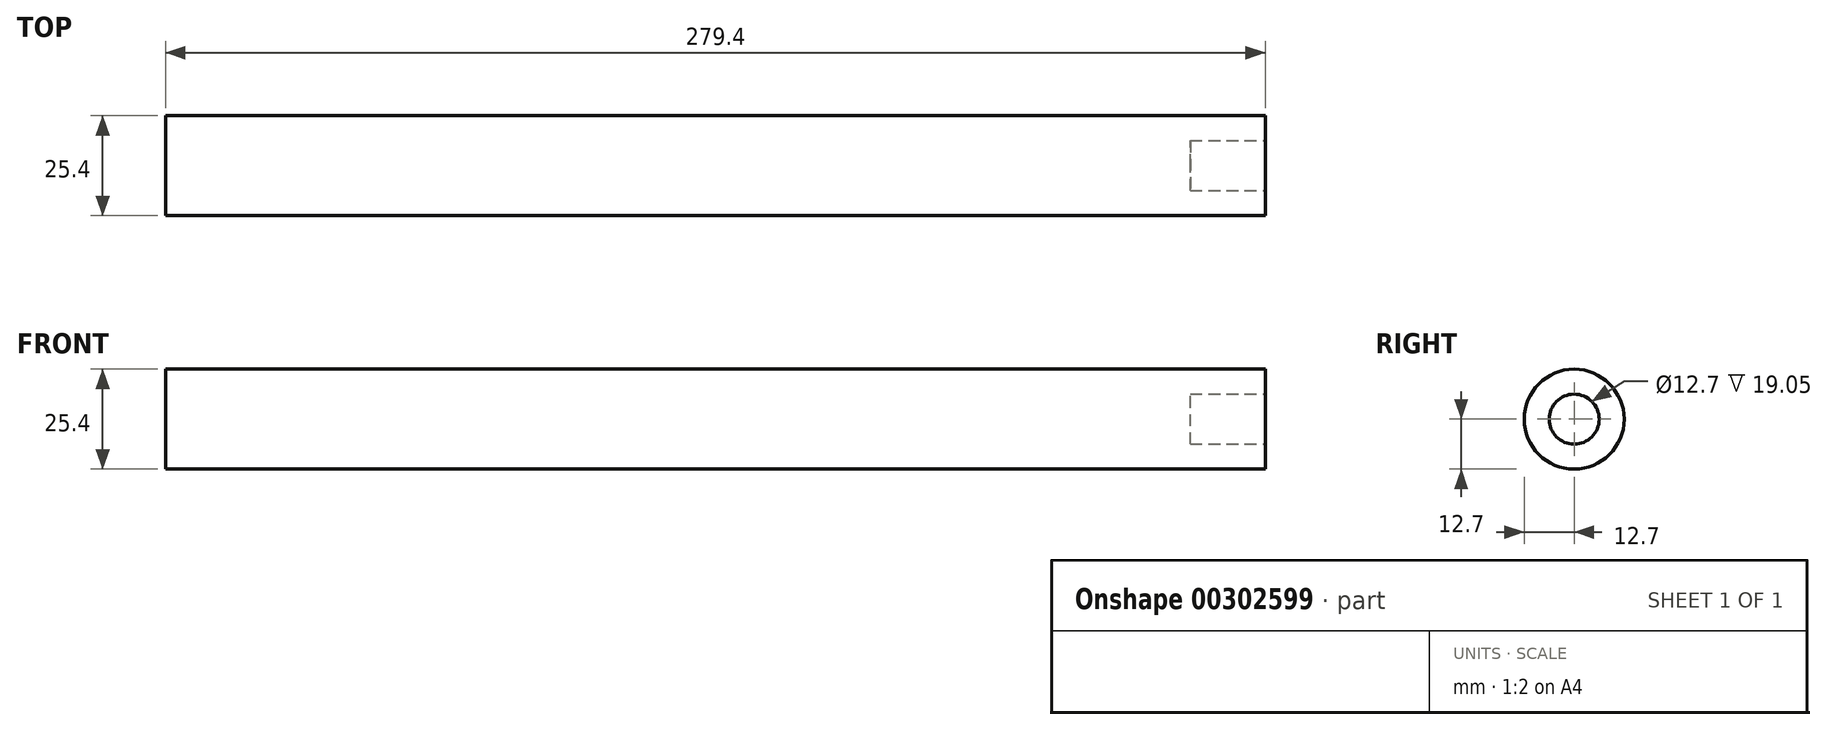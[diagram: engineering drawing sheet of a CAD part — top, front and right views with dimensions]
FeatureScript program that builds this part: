
annotation { "Feature Type Name" : "Feature", "Feature Type Description" : "" }
export const myFeature = defineFeature(function(context is Context, id is Id, definition is map)
    precondition{}
    {
        {
            var Q0;
            Q0=qCreatedBy(makeId("Right.planeOp"),FACE);
            var sketch = newSketch(context, id + "F0", { "sketchPlane" : qUnion([Q0])});
            skCircle(sketch, "E0", {"center": v(0, 0) * mm, "radius": 12.7 * mm});
            skSolve(sketch);
        }
        {
            var Q0;
            Q0=makeQuery(id+"F0.imprint","IMPRINT",FACE,{"disambiguationData":[TD([[makeQuery(id+"F0.imprint","IMPRINT",EDGE,{"derivedFrom":sQuery(id+"F0.wireOp",EDGE,"E0")}),1.0]])]});
            extrude(context, id + "F1", {"entities" : qUnion([Q0]), "depth" : 279.4 * mm});
        }
        {
            var Q0;
            Q0=makeQuery(id+"F1.opExtrude","CAP_FACE",FACE,{"disambiguationData":[OSD([sQuery(id+"F0.wireOp",EDGE,"E0")])],"isStart":false});
            var sketch = newSketch(context, id + "F2", { "sketchPlane" : qUnion([Q0])});
            skCircle(sketch, "E1", {"center": v(0, 0) * mm, "radius": 6.35 * mm});
            skSolve(sketch);
        }
        {
            var Q0;
            Q0=makeQuery(id+"F2.imprint","IMPRINT",FACE,{"disambiguationData":[TD([[makeQuery(id+"F2.imprint","IMPRINT",EDGE,{"derivedFrom":sQuery(id+"F2.wireOp",EDGE,"E1")}),1.0]])]});
            extrude(context, id + "F3", {"entities" : qUnion([Q0]), "operationType" : NewBodyOperationType.REMOVE, "oppositeDirection" : true, "depth" : 19.05 * mm});
        }
        {
            var Q0;
            Q0=makeQuery(id+"F1.opExtrude","CAP_FACE",FACE,{"disambiguationData":[OSD([sQuery(id+"F0.wireOp",EDGE,"E0")])],"isStart":false});
            var sketch = newSketch(context, id + "F4", { "sketchPlane" : qUnion([Q0])});
            skLineSegment(sketch, "E2.bottom", {"start": v(-2.54, 12.7) * mm, "end": v(2.54, 12.7) * mm});
            skLineSegment(sketch, "E2.top", {"start": v(-2.54, -19.69) * mm, "end": v(2.54, -19.69) * mm});
            skLineSegment(sketch, "E2.left", {"start": v(-2.54, 12.7) * mm, "end": v(-2.54, -19.69) * mm});
            skLineSegment(sketch, "E2.right", {"start": v(2.54, 12.7) * mm, "end": v(2.54, -19.69) * mm});
            skLineSegment(sketch, "E3.bottom", {"start": v(-12.7, 2.54) * mm, "end": v(19.69, 2.54) * mm});
            skLineSegment(sketch, "E3.top", {"start": v(-12.7, -2.54) * mm, "end": v(19.69, -2.54) * mm});
            skLineSegment(sketch, "E3.left", {"start": v(-12.7, 2.54) * mm, "end": v(-12.7, -2.54) * mm});
            skLineSegment(sketch, "E3.right", {"start": v(19.69, 2.54) * mm, "end": v(19.69, -2.54) * mm});
            skSolve(sketch);
        }
        {
            var Q0;
            {var subQ0=makeQuery(id+"F1.opExtrude","CAP_EDGE",EDGE,{"disambiguationData":[OSD([sQuery(id+"F0.wireOp",EDGE,"E0")])],"isStart":false});var subQ2=sQuery(id+"F4.wireOp",EDGE,"E2.left");var subQ3=makeQuery(id+"F4.imprint","INTERSECT",VERTEX,{"disambiguationData":[OD(0.0)],"derivedFrom":[subQ0,subQ2]});Q0=makeQuery(id+"F4.imprint","IMPRINT",FACE,{"disambiguationData":[TD([[makeQuery(id+"F4.imprint","IMPRINT",EDGE,{"disambiguationData":[TD([[subQ3,-1.0]])],"derivedFrom":subQ2}),1.0]])]});}
            var Q1;
            {var subQ0=sQuery(id+"F4.wireOp",EDGE,"E3.bottom");var subQ1=makeQuery(id+"F1.opExtrude","CAP_EDGE",EDGE,{"disambiguationData":[OSD([sQuery(id+"F0.wireOp",EDGE,"E0")])],"isStart":false});var subQ2=makeQuery(id+"F4.imprint","INTERSECT",VERTEX,{"disambiguationData":[OD(0.0)],"derivedFrom":[subQ1,subQ0]});Q1=makeQuery(id+"F4.imprint","IMPRINT",FACE,{"disambiguationData":[TD([[makeQuery(id+"F4.imprint","IMPRINT",EDGE,{"disambiguationData":[TD([[subQ2,-1.0]])],"derivedFrom":subQ0}),-1.0]])]});}
            var Q2;
            {var subQ0=sQuery(id+"F4.wireOp",EDGE,"E2.left");var subQ1=makeQuery(id+"F1.opExtrude","CAP_EDGE",EDGE,{"disambiguationData":[OSD([sQuery(id+"F0.wireOp",EDGE,"E0")])],"isStart":false});var subQ2=makeQuery(id+"F4.imprint","INTERSECT",VERTEX,{"disambiguationData":[OD(1.0)],"derivedFrom":[subQ1,subQ0]});Q2=makeQuery(id+"F4.imprint","IMPRINT",FACE,{"disambiguationData":[TD([[makeQuery(id+"F4.imprint","IMPRINT",EDGE,{"disambiguationData":[TD([[subQ2,1.0]])],"derivedFrom":subQ0}),1.0]])]});}
            var Q3;
            {var subQ0=sQuery(id+"F4.wireOp",EDGE,"E3.bottom");var subQ1=makeQuery(id+"F1.opExtrude","CAP_EDGE",EDGE,{"disambiguationData":[OSD([sQuery(id+"F0.wireOp",EDGE,"E0")])],"isStart":false});var subQ2=makeQuery(id+"F4.imprint","INTERSECT",VERTEX,{"disambiguationData":[OD(1.0)],"derivedFrom":[subQ1,subQ0]});Q3=makeQuery(id+"F4.imprint","IMPRINT",FACE,{"disambiguationData":[TD([[makeQuery(id+"F4.imprint","IMPRINT",EDGE,{"disambiguationData":[TD([[subQ2,1.0]])],"derivedFrom":subQ0}),-1.0]])]});}
            var Q4;
            {var subQ0=sQuery(id+"F4.wireOp",EDGE,"E3.bottom");var subQ1=sQuery(id+"F4.wireOp",EDGE,"E2.right");var subQ2=makeQuery(id+"F4.imprint","INTERSECT",VERTEX,{"derivedFrom":[subQ1,subQ0]});Q4=makeQuery(id+"F4.imprint","IMPRINT",FACE,{"disambiguationData":[TD([[makeQuery(id+"F4.imprint","IMPRINT",EDGE,{"disambiguationData":[TD([[subQ2,-1.0]])],"derivedFrom":subQ1}),1.0]])]});}
            var Q5;
            {var subQ0=sQuery(id+"F4.wireOp",EDGE,"E3.bottom");var subQ1=sQuery(id+"F4.wireOp",EDGE,"E2.left");var subQ2=makeQuery(id+"F4.imprint","INTERSECT",VERTEX,{"derivedFrom":[subQ1,subQ0]});Q5=makeQuery(id+"F4.imprint","IMPRINT",FACE,{"disambiguationData":[TD([[makeQuery(id+"F4.imprint","IMPRINT",EDGE,{"disambiguationData":[TD([[subQ2,-1.0]])],"derivedFrom":subQ1}),-1.0]])]});}
            var Q6;
            {var subQ0=sQuery(id+"F4.wireOp",EDGE,"E3.bottom");var subQ1=sQuery(id+"F4.wireOp",EDGE,"E2.left");var subQ2=makeQuery(id+"F4.imprint","INTERSECT",VERTEX,{"derivedFrom":[subQ1,subQ0]});Q6=makeQuery(id+"F4.imprint","IMPRINT",FACE,{"disambiguationData":[TD([[makeQuery(id+"F4.imprint","IMPRINT",EDGE,{"disambiguationData":[TD([[subQ2,1.0]])],"derivedFrom":subQ1}),1.0]])]});}
            var Q7;
            {var subQ0=sQuery(id+"F4.wireOp",EDGE,"E3.top");var subQ1=sQuery(id+"F4.wireOp",EDGE,"E2.left");var subQ2=makeQuery(id+"F4.imprint","INTERSECT",VERTEX,{"derivedFrom":[subQ1,subQ0]});Q7=makeQuery(id+"F4.imprint","IMPRINT",FACE,{"disambiguationData":[TD([[makeQuery(id+"F4.imprint","IMPRINT",EDGE,{"disambiguationData":[TD([[subQ2,-1.0]])],"derivedFrom":subQ1}),1.0]])]});}
            extrude(context, id + "F5", {"entities" : qUnion([Q0, Q1, Q2, Q3, Q4, Q5, Q6, Q7]), "operationType" : NewBodyOperationType.REMOVE, "oppositeDirection" : true, "depth" : 2.54 * mm});
        }
    });
